# Revit family: Hager-Orion_Plus-IP65-D300-Cl.II-Poly_floor_encl-630A-NoHosted-PT-pt
name_source: partatom
category: Electrical Equipment
units: mm (PartAtom-declared; Revit-internal decimal feet)

## family parameters
Always vertical = Yes
Cut with Voids When Loaded = No
Panel Configuration = Two Columns, Circuits Across
Part Type = Panelboard
Room Calculation Point = No
Round Connector Dimension = Use Diameter
Shared = No
Work Plane-Based = Yes

## types (18) — shared parameters
Default Elevation = 1219 mm
EF000003 - Método de montagem = EV012274 - Instalação de piso
EF000007 - Cor = EV000270 - Cinzento
EF000049 - Profundidade = 300 mm  [stored 0.984252 ft]
EF000116 - Número RAL = 7035
EF000118 - Com tampa de montagem = No
EF001596 - Material do corpo = EV000139 - Plástico
EF001613 - Integridade do circuito = EV000494 - Nenhum
EF003532 - Adequado para uso no exterior = Yes
EF004464 - Tipo de porta = EV002646 - Único
EF005474 - Grau de proteção (IP) = EV006421 - IP65
EF006306 - Com fecho = Yes
EF007800 - Adequado para proteção contra raios = No
EF008873 - Corrente nominal (In) = 630 A
EF009170 - Espessura do material do invólucro = 2 mm  [stored 0.00656168 ft]
EF009171 - Espessura do material da porta/tampa = 2 mm  [stored 0.00656168 ft]
EF015940 - Tampa com libertação de sobrepressão = No
HG000002 - Com porta ou tampa = Yes
HG000003 - Gama = Orion Plus
HG000006 - Encastrado = No
HG000009 - Porta dupla = No
HG000010 - Portas assimétricas = No
HG000023 - Recinto de secção dupla = No
HG000024 - Altura da secção inferior = 600 mm
HG000026 - Instalação no chão = Yes
HG000027 - Altura da Plinta = 70 mm  [stored 0.229659 ft]
Manufacturer = Hager
Type Comments = Orion Plus
zero-valued in all types: EF000218 - Profundidade incorporada, EF000437 - Número de entradas de condutores, EF002950 - Largura em número de módulos, EF009554 - Número de aberturas para placas de flange

## per-type parameters (varying)
| type | EF000008 - Largura | EF000040 - Altura | EF000266 - Número de linhas | EF000339 - Tipo de difusor | EF001088 - Extensão possível | EF001131 - Profundidade interior | EF004293 - Força de impacto | EF004427 - Número de módulos | EF006244 - Tampa/porta transparente | EF009212 - Tipo de tampa | HG000004 - Referência do Fabricante |
| Instalação de piso IP65 L1100 A1200 P300  - FL332B | 1100 mm | 1200 mm | 7 | EV004216 - Porta | Yes | 300 mm  [stored 0.984252 ft] | EV008784 - IK10 | 322 | Yes | EV009916 - Com recuo | FL332B |
| Instalação de piso IP65 L1100 A1200 P300  - FL532B | 1100 mm | 1200 mm | 7 | EV004216 - Porta | Yes | 300 mm  [stored 0.984252 ft] | EV008784 - IK10 | 322 | Yes | EV000116 - Fechado | FL532B |
| Instalação de piso IP65 L1100 A600 P300  - FL330B | 1100 mm | 600 mm | 3 | EV004216 - Porta | Yes | 300 mm  [stored 0.984252 ft] | EV008784 - IK10 | 138 | Yes | EV009916 - Com recuo | FL330B |
| Instalação de piso IP65 L1100 A600 P300  - FL530B | 1100 mm | 600 mm | 3 | EV004216 - Porta | Yes | 300 mm  [stored 0.984252 ft] | EV008784 - IK10 | 138 | Yes | EV000116 - Fechado | FL530B |
| Instalação de piso IP65 L1100 A900 P300  - FL331B | 1100 mm | 900 mm  [stored 2.95276 ft] | 5 | EV004216 - Porta | Yes | 300 mm  [stored 0.984252 ft] | EV008784 - IK10 | 230 | Yes | EV009916 - Com recuo | FL331B |
| Instalação de piso IP65 L1100 A900 P300  - FL531B | 1100 mm | 900 mm  [stored 2.95276 ft] | 5 | EV004216 - Porta | Yes | 300 mm  [stored 0.984252 ft] | EV008784 - IK10 | 230 | Yes | EV000116 - Fechado | FL531B |
| Instalação de piso IP65 L600 A1200 P300  - FL322B | 600 mm | 1200 mm | 7 | EV004216 - Porta | Yes | 300 mm  [stored 0.984252 ft] | EV008784 - IK10 | 161 | Yes | EV009916 - Com recuo | FL322B |
| Instalação de piso IP65 L600 A1200 P300  - FL522B | 600 mm | 1200 mm | 7 | EV004216 - Porta | Yes | 300 mm  [stored 0.984252 ft] | EV008784 - IK10 | 161 | Yes | EV000116 - Fechado | FL522B |
| Instalação de piso IP65 L600 A600 P300  - FL320B | 600 mm | 600 mm | 3 | EV004216 - Porta | Yes | 200 mm  [stored 0.656168 ft] | EV008784 - IK10 | 69 | Yes | EV009916 - Com recuo | FL320B |
| Instalação de piso IP65 L600 A600 P300  - FL520B | 600 mm | 600 mm | 3 | EV004216 - Porta | Yes | 300 mm  [stored 0.984252 ft] | EV008784 - IK10 | 69 | Yes | EV000116 - Fechado | FL520B |
| Instalação de piso IP65 L600 A900 P300  - FL321B | 600 mm | 900 mm  [stored 2.95276 ft] | 5 | EV004216 - Porta | Yes | 300 mm  [stored 0.984252 ft] | EV008784 - IK10 | 115 | Yes | EV009916 - Com recuo | FL321B |
| Instalação de piso IP65 L600 A900 P300  - FL521B | 600 mm | 900 mm  [stored 2.95276 ft] | 5 | EV004216 - Porta | Yes | 300 mm  [stored 0.984252 ft] | EV008784 - IK10 | 115 | Yes | EV000116 - Fechado | FL521B |
| Instalação de piso IP65 L850 A1200 P300  - FL327B | 850 mm  [stored 2.78871 ft] | 1200 mm | 7 | EV001012 - Tampa | No | 300 mm  [stored 0.984252 ft] | EV006814 - IK08 | 259 | No | EV000116 - Fechado | FL327B |
| Instalação de piso IP65 L850 A1200 P300  - FL527B | 850 mm  [stored 2.78871 ft] | 1200 mm | 7 | EV004216 - Porta | No | 235 mm  [stored 0.770997 ft] | EV008784 - IK10 | 259 | No | EV009916 - Com recuo | FL527B |
| Instalação de piso IP65 L850 A600 P300  - FL325B | 850 mm  [stored 2.78871 ft] | 600 mm | 3 | EV004216 - Porta | Yes | 300 mm  [stored 0.984252 ft] | EV008784 - IK10 | 111 | Yes | EV009916 - Com recuo | FL325B |
| Instalação de piso IP65 L850 A600 P300  - FL525B | 850 mm  [stored 2.78871 ft] | 600 mm | 3 | EV004216 - Porta | Yes | 300 mm  [stored 0.984252 ft] | EV008784 - IK10 | 111 | Yes | EV000116 - Fechado | FL525B |
| Instalação de piso IP65 L850 A900 P300  - FL326B | 850 mm  [stored 2.78871 ft] | 900 mm  [stored 2.95276 ft] | 5 | EV004216 - Porta | Yes | 300 mm  [stored 0.984252 ft] | EV008784 - IK10 | 185 | Yes | EV009916 - Com recuo | FL326B |
| Instalação de piso IP65 L850 A900 P300  - FL526B | 850 mm  [stored 2.78871 ft] | 900 mm  [stored 2.95276 ft] | 5 | EV004216 - Porta | Yes | 300 mm  [stored 0.984252 ft] | EV008784 - IK10 | 185 | Yes | EV000116 - Fechado | FL526B |

note: [stored X ft] marks values corroborated as IEEE doubles in the binary element streams (Revit-internal decimal feet)

## geometry (parser evidence)
native form markers: Blend x4, Sweep x5
no freeform markers — native parametric forms only
